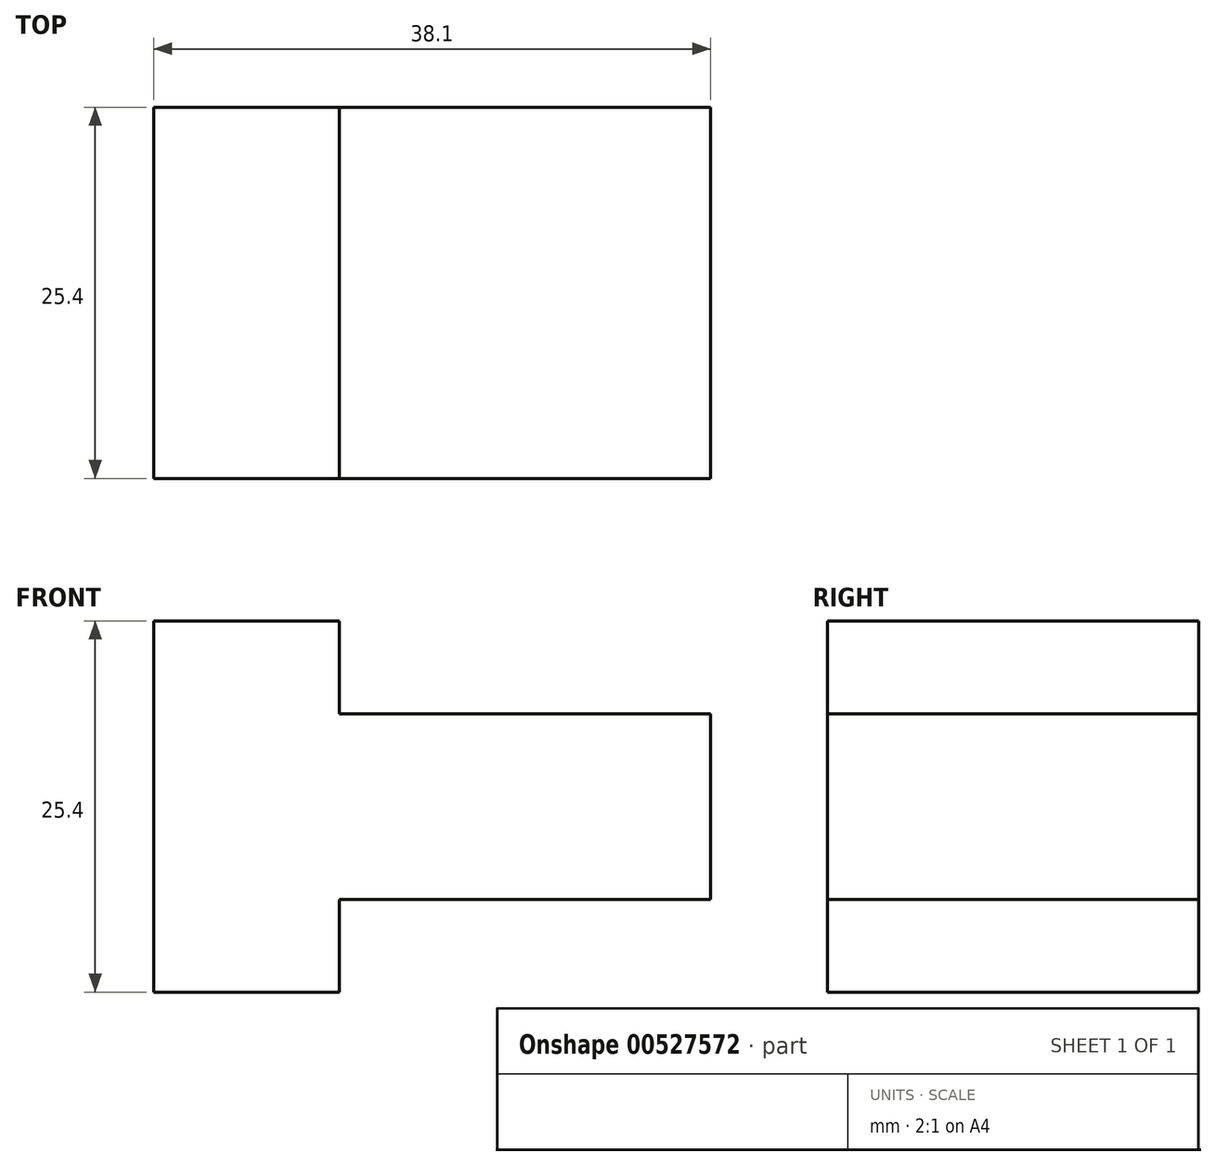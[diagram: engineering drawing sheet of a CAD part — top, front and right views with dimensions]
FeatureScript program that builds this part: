
annotation { "Feature Type Name" : "Feature", "Feature Type Description" : "" }
export const myFeature = defineFeature(function(context is Context, id is Id, definition is map)
    precondition{}
    {
        {
            var Q0;
            Q0=qCreatedBy(makeId("Front.planeOp"),FACE);
            var sketch = newSketch(context, id + "F0", { "sketchPlane" : qUnion([Q0])});
            skLineSegment(sketch, "E0", {"start": v(0, 0) * mm, "end": v(12.7, 0) * mm});
            skLineSegment(sketch, "E1", {"start": v(12.7, 0) * mm, "end": v(12.7, 6.35) * mm});
            skLineSegment(sketch, "E2", {"start": v(12.7, 6.35) * mm, "end": v(38.1, 6.35) * mm});
            skLineSegment(sketch, "E3", {"start": v(38.1, 6.35) * mm, "end": v(38.1, 19.05) * mm});
            skLineSegment(sketch, "E4", {"start": v(38.1, 19.05) * mm, "end": v(12.7, 19.05) * mm});
            skLineSegment(sketch, "E5", {"start": v(12.7, 18.85) * mm, "end": v(12.7, 19.05) * mm});
            skLineSegment(sketch, "E6", {"start": v(12.7, 19.05) * mm, "end": v(12.7, 25.4) * mm});
            skLineSegment(sketch, "E7", {"start": v(12.7, 25.4) * mm, "end": v(0, 25.4) * mm});
            skLineSegment(sketch, "E8", {"start": v(0, 25.4) * mm, "end": v(0, 0) * mm});
            skLineSegment(sketch, "E9", {"start": v(12.7, 25.4) * mm, "end": v(12.7, 19.05) * mm});
            skSolve(sketch);
        }
        {
            var Q0;
            Q0=makeQuery(id+"F0.imprint","IMPRINT",FACE,{"disambiguationData":[TD([[makeQuery(id+"F0.imprint","IMPRINT",EDGE,{"derivedFrom":sQuery(id+"F0.wireOp",EDGE,"E0")}),1.0]])]});
            extrude(context, id + "F1", {"entities" : qUnion([Q0]), "depth" : 25.4 * mm, "offsetDistance" : 25.4 * mm});
        }
    });
